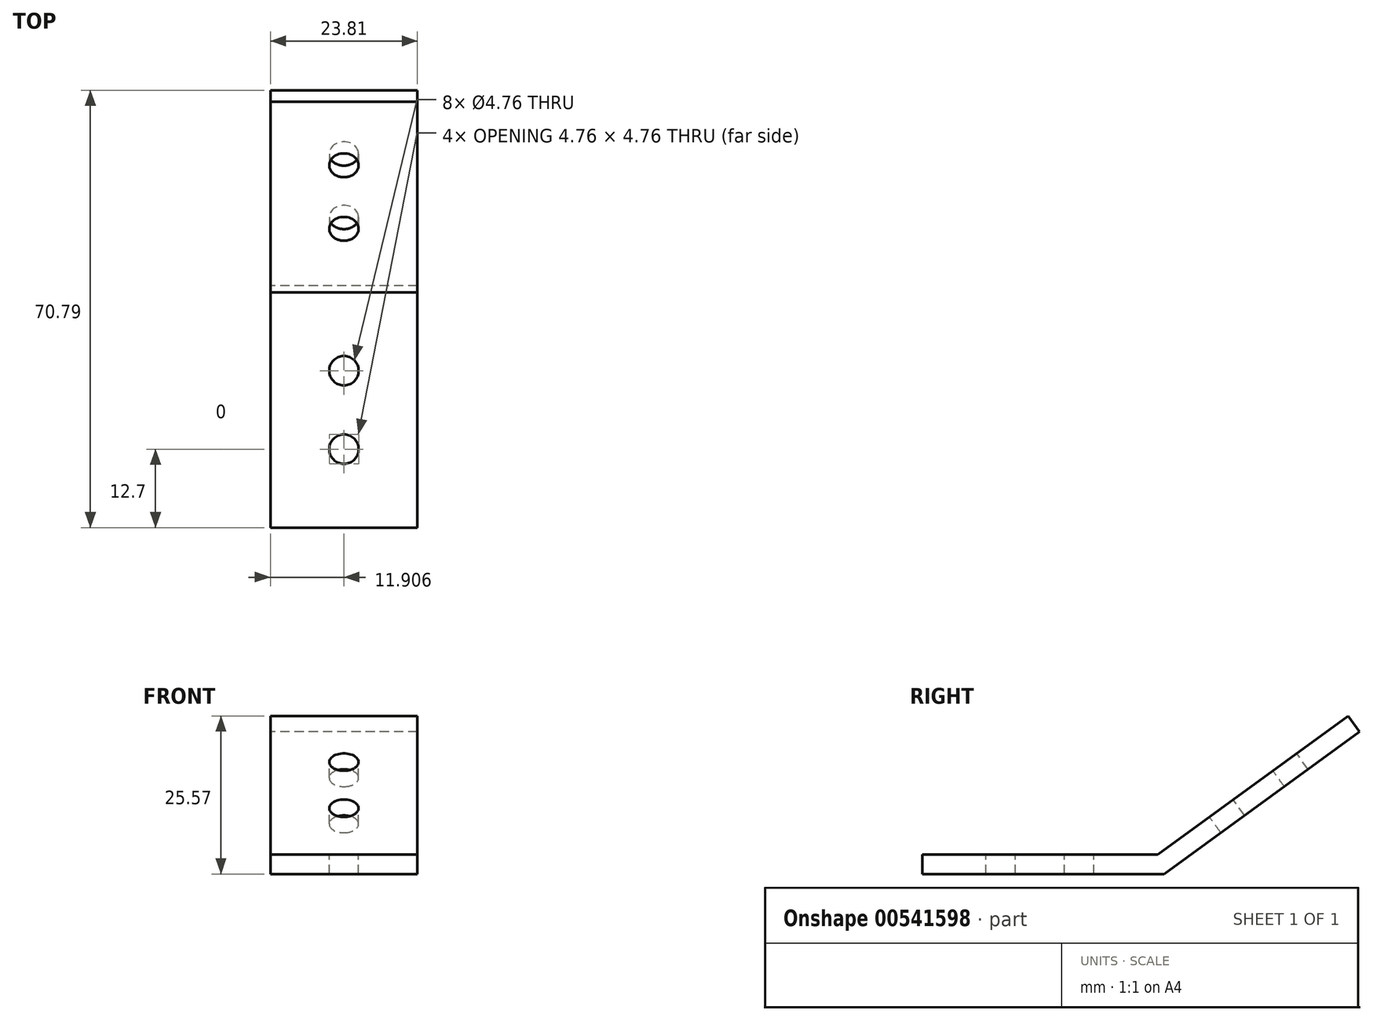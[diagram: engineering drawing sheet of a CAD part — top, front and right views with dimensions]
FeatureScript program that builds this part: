
annotation { "Feature Type Name" : "Feature", "Feature Type Description" : "" }
export const myFeature = defineFeature(function(context is Context, id is Id, definition is map)
    precondition{}
    {
        {
            var Q0;
            Q0=qCreatedBy(makeId("Right.planeOp"),FACE);
            var sketch = newSketch(context, id + "F0", { "sketchPlane" : qUnion([Q0])});
            skLineSegment(sketch, "E0", {"start": v(0, 0) * mm, "end": v(-38.1, 0) * mm});
            skLineSegment(sketch, "E1", {"start": v(0, 0) * mm, "end": v(30.82, 22.4) * mm});
            skLineSegment(sketch, "E2.0", {"start": v(1.03, -3.18) * mm, "end": v(32.69, 19.83) * mm});
            skLineSegment(sketch, "E2.1", {"start": v(1.03, -3.17) * mm, "end": v(-38.1, -3.18) * mm});
            skLineSegment(sketch, "E3", {"start": v(-38.1, 0) * mm, "end": v(-38.1, -3.18) * mm});
            skLineSegment(sketch, "E4", {"start": v(30.82, 22.4) * mm, "end": v(32.69, 19.83) * mm});
            skSolve(sketch);
        }
        {
            var Q0;
            Q0 = qSketchRegion(id + "F0", true);
            extrude(context, id + "F1", {"entities" : qUnion([Q0]), "depth" : 23.8 * mm, "offsetDistance" : 25.4 * mm});
        }
        {
            var Q0;
            Q0=makeQuery(id+"F1.opExtrude","SWEPT_FACE",FACE,{"disambiguationData":[OSD([sQuery(id+"F0.wireOp",EDGE,"E0")])]});
            var sketch = newSketch(context, id + "F2", { "sketchPlane" : qUnion([Q0])});
            skLineSegment(sketch, "E5", {"start": v(11.9, -38.1) * mm, "end": v(11.9, 0) * mm});
            skPoint(sketch, "E6", {"position": v(11.9, -25.4) * mm});
            skPoint(sketch, "E7", {"position": v(11.9, -12.7) * mm});
            skCircle(sketch, "E8", {"center": v(11.9, -12.7) * mm, "radius": 2.38 * mm});
            skCircle(sketch, "E9", {"center": v(11.9, -25.4) * mm, "radius": 2.38 * mm});
            skSolve(sketch);
        }
        {
            var Q0;
            Q0 = qSketchRegion(id + "F2", true);
            extrude(context, id + "F3", {"entities" : qUnion([Q0]), "operationType" : NewBodyOperationType.REMOVE, "oppositeDirection" : true, "depth" : 25.4 * mm, "offsetDistance" : 25.4 * mm});
        }
        {
            var Q0;
            Q0=makeQuery(id+"F1.opExtrude","SWEPT_FACE",FACE,{"disambiguationData":[OSD([sQuery(id+"F0.wireOp",EDGE,"E1")])]});
            var sketch = newSketch(context, id + "F4", { "sketchPlane" : qUnion([Q0])});
            skLineSegment(sketch, "E10", {"start": v(11.9, 0) * mm, "end": v(11.9, 38.1) * mm});
            skPoint(sketch, "E11", {"position": v(11.9, 12.7) * mm});
            skPoint(sketch, "E12", {"position": v(11.9, 25.4) * mm});
            skCircle(sketch, "E13", {"center": v(11.9, 12.7) * mm, "radius": 2.38 * mm});
            skCircle(sketch, "E14", {"center": v(11.9, 25.4) * mm, "radius": 2.38 * mm});
            skSolve(sketch);
        }
        {
            var Q0;
            Q0 = qSketchRegion(id + "F4", true);
            extrude(context, id + "F5", {"entities" : qUnion([Q0]), "operationType" : NewBodyOperationType.REMOVE, "oppositeDirection" : true, "depth" : 25.4 * mm, "offsetDistance" : 25.4 * mm});
        }
    });
